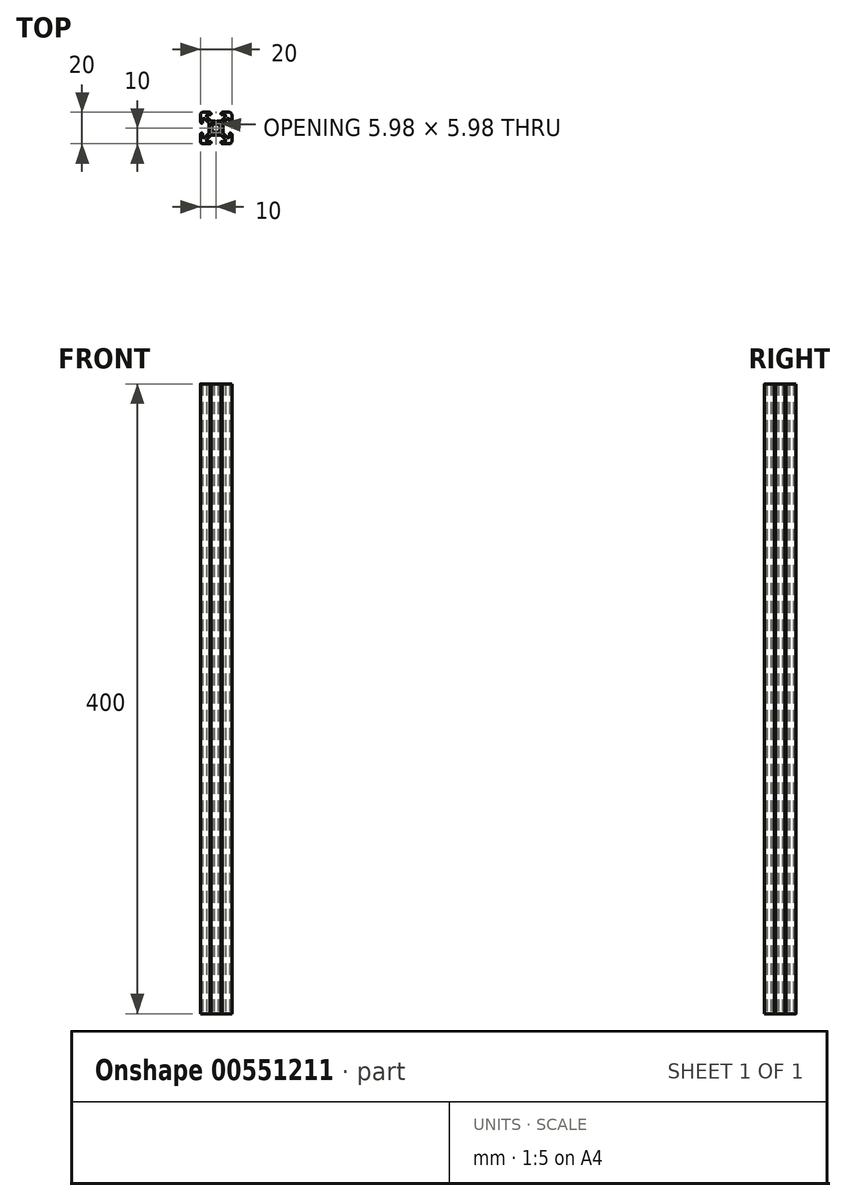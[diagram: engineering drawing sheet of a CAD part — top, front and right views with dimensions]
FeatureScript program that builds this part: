
annotation { "Feature Type Name" : "Feature", "Feature Type Description" : "" }
export const myFeature = defineFeature(function(context is Context, id is Id, definition is map)
    precondition{}
    {
        {
            var Q0;
            Q0=qCreatedBy(makeId("Top.planeOp"),FACE);
            var sketch = newSketch(context, id + "F0", { "sketchPlane" : qUnion([Q0])});
            skLineSegment(sketch, "E0.0", {"start": v(-0.95, 4.5) * mm, "end": v(-3.23, 4.5) * mm});
            skLineSegment(sketch, "E0.1", {"start": v(-3.59, 4.65) * mm, "end": v(-5.85, 6.91) * mm});
            skArc(sketch, "E0.2", {"start": v(-3.23, 4.5) * mm, "mid": v(-3.42, 4.54) * mm, "end": v(-3.59, 4.65) * mm});
            skArc(sketch, "E0.3", {"start": v(-4.65, 3.59) * mm, "mid": v(-4.54, 3.42) * mm, "end": v(-4.5, 3.23) * mm});
            skLineSegment(sketch, "E0.4", {"start": v(-6.91, 5.85) * mm, "end": v(-4.65, 3.59) * mm});
            skArc(sketch, "E0.5", {"start": v(-5.85, 6.91) * mm, "mid": v(-5.96, 7.08) * mm, "end": v(-6, 7.27) * mm});
            skLineSegment(sketch, "E0.6", {"start": v(-6, 7.27) * mm, "end": v(-6, 8) * mm});
            skArc(sketch, "E0.7", {"start": v(-6, 8) * mm, "mid": v(-5.85, 8.35) * mm, "end": v(-5.5, 8.5) * mm});
            skLineSegment(sketch, "E0.8", {"start": v(-5.5, 8.5) * mm, "end": v(-3.6, 8.5) * mm});
            skArc(sketch, "E0.9", {"start": v(-3.6, 8.5) * mm, "mid": v(-3.25, 8.65) * mm, "end": v(-3.1, 9) * mm});
            skLineSegment(sketch, "E0.10", {"start": v(-3.1, 9) * mm, "end": v(-3.1, 9.3) * mm});
            skArc(sketch, "E0.11", {"start": v(-3.1, 9.3) * mm, "mid": v(-3.16, 9.44) * mm, "end": v(-3.3, 9.5) * mm});
            skLineSegment(sketch, "E0.12", {"start": v(-3.3, 9.5) * mm, "end": v(-3.65, 9.5) * mm});
            skLineSegment(sketch, "E0.13", {"start": v(-3.65, 9.5) * mm, "end": v(-3.65, 9.8) * mm});
            skArc(sketch, "E0.14", {"start": v(-3.65, 9.8) * mm, "mid": v(-3.7, 9.94) * mm, "end": v(-3.85, 10) * mm});
            skLineSegment(sketch, "E0.15", {"start": v(-3.85, 10) * mm, "end": v(-8.5, 10) * mm});
            skArc(sketch, "E0.16", {"start": v(-7.27, 6) * mm, "mid": v(-7.08, 5.96) * mm, "end": v(-6.91, 5.85) * mm});
            skLineSegment(sketch, "E0.17", {"start": v(-8, 6) * mm, "end": v(-7.27, 6) * mm});
            skArc(sketch, "E0.18", {"start": v(-8.5, 5.5) * mm, "mid": v(-8.35, 5.85) * mm, "end": v(-8, 6) * mm});
            skLineSegment(sketch, "E0.19", {"start": v(-8.5, 3.6) * mm, "end": v(-8.5, 5.5) * mm});
            skArc(sketch, "E0.20", {"start": v(-9, 3.1) * mm, "mid": v(-8.65, 3.25) * mm, "end": v(-8.5, 3.6) * mm});
            skArc(sketch, "E0.21", {"start": v(-8.5, 10) * mm, "mid": v(-9.56, 9.56) * mm, "end": v(-10, 8.5) * mm});
            skLineSegment(sketch, "E0.22", {"start": v(-10, 8.5) * mm, "end": v(-10, 3.85) * mm});
            skArc(sketch, "E0.23", {"start": v(-10, 3.85) * mm, "mid": v(-9.94, 3.7) * mm, "end": v(-9.8, 3.65) * mm});
            skLineSegment(sketch, "E0.24", {"start": v(-9.8, 3.65) * mm, "end": v(-9.5, 3.65) * mm});
            skLineSegment(sketch, "E0.25", {"start": v(-9.5, 3.65) * mm, "end": v(-9.5, 3.3) * mm});
            skArc(sketch, "E0.26", {"start": v(-9.5, 3.3) * mm, "mid": v(-9.44, 3.16) * mm, "end": v(-9.3, 3.1) * mm});
            skLineSegment(sketch, "E0.27", {"start": v(-9.3, 3.1) * mm, "end": v(-9, 3.1) * mm});
            skLineSegment(sketch, "E0.28", {"start": v(-4.5, 3.23) * mm, "end": v(-4.5, 0.95) * mm});
            skLineSegment(sketch, "E0.29", {"start": v(-0.1, 4.04) * mm, "end": v(-0.85, 4.47) * mm});
            skArc(sketch, "E0.30", {"start": v(-0.85, 4.47) * mm, "mid": v(-0.9, 4.5) * mm, "end": v(-0.95, 4.5) * mm});
            skLineSegment(sketch, "E0.31", {"start": v(0.85, 4.47) * mm, "end": v(0.1, 4.04) * mm});
            skLineSegment(sketch, "E0.32", {"start": v(3.23, 4.5) * mm, "end": v(0.95, 4.5) * mm});
            skArc(sketch, "E0.33", {"start": v(0.95, 4.5) * mm, "mid": v(0.9, 4.5) * mm, "end": v(0.85, 4.47) * mm});
            skArc(sketch, "E0.34", {"start": v(0.1, 4.04) * mm, "mid": v(0, 4.01) * mm, "end": v(-0.1, 4.04) * mm});
            skLineSegment(sketch, "E0.35", {"start": v(5.85, 6.91) * mm, "end": v(3.59, 4.65) * mm});
            skLineSegment(sketch, "E0.36", {"start": v(6, 8) * mm, "end": v(6, 7.27) * mm});
            skArc(sketch, "E0.37", {"start": v(5.5, 8.5) * mm, "mid": v(5.85, 8.35) * mm, "end": v(6, 8) * mm});
            skLineSegment(sketch, "E0.38", {"start": v(3.6, 8.5) * mm, "end": v(5.5, 8.5) * mm});
            skArc(sketch, "E0.39", {"start": v(3.1, 9) * mm, "mid": v(3.25, 8.65) * mm, "end": v(3.6, 8.5) * mm});
            skLineSegment(sketch, "E0.40", {"start": v(8.5, 10) * mm, "end": v(3.85, 10) * mm});
            skArc(sketch, "E0.41", {"start": v(3.59, 4.65) * mm, "mid": v(3.42, 4.54) * mm, "end": v(3.23, 4.5) * mm});
            skArc(sketch, "E0.42", {"start": v(6, 7.27) * mm, "mid": v(5.96, 7.08) * mm, "end": v(5.85, 6.91) * mm});
            skLineSegment(sketch, "E0.43", {"start": v(3.1, 9.3) * mm, "end": v(3.1, 9) * mm});
            skArc(sketch, "E0.44", {"start": v(3.85, 10) * mm, "mid": v(3.7, 9.94) * mm, "end": v(3.65, 9.8) * mm});
            skLineSegment(sketch, "E0.45", {"start": v(3.65, 9.8) * mm, "end": v(3.65, 9.5) * mm});
            skLineSegment(sketch, "E0.46", {"start": v(3.65, 9.5) * mm, "end": v(3.3, 9.5) * mm});
            skArc(sketch, "E0.47", {"start": v(3.3, 9.5) * mm, "mid": v(3.16, 9.44) * mm, "end": v(3.1, 9.3) * mm});
            skArc(sketch, "E0.48", {"start": v(10, 8.5) * mm, "mid": v(9.56, 9.56) * mm, "end": v(8.5, 10) * mm});
            skLineSegment(sketch, "E0.49", {"start": v(10, 3.85) * mm, "end": v(10, 8.5) * mm});
            skArc(sketch, "E0.50", {"start": v(9.8, 3.65) * mm, "mid": v(9.94, 3.7) * mm, "end": v(10, 3.85) * mm});
            skLineSegment(sketch, "E0.51", {"start": v(9.5, 3.65) * mm, "end": v(9.8, 3.65) * mm});
            skLineSegment(sketch, "E0.52", {"start": v(9.5, 3.3) * mm, "end": v(9.5, 3.65) * mm});
            skArc(sketch, "E0.53", {"start": v(9.3, 3.1) * mm, "mid": v(9.44, 3.16) * mm, "end": v(9.5, 3.3) * mm});
            skArc(sketch, "E0.54", {"start": v(8.5, 3.6) * mm, "mid": v(8.65, 3.25) * mm, "end": v(9, 3.1) * mm});
            skLineSegment(sketch, "E0.55", {"start": v(8.5, 5.5) * mm, "end": v(8.5, 3.6) * mm});
            skArc(sketch, "E0.56", {"start": v(8, 6) * mm, "mid": v(8.35, 5.85) * mm, "end": v(8.5, 5.5) * mm});
            skLineSegment(sketch, "E0.57", {"start": v(7.27, 6) * mm, "end": v(8, 6) * mm});
            skArc(sketch, "E0.58", {"start": v(6.91, 5.85) * mm, "mid": v(7.08, 5.96) * mm, "end": v(7.27, 6) * mm});
            skLineSegment(sketch, "E0.59", {"start": v(4.65, 3.59) * mm, "end": v(6.91, 5.85) * mm});
            skArc(sketch, "E0.60", {"start": v(4.5, 3.23) * mm, "mid": v(4.54, 3.42) * mm, "end": v(4.65, 3.59) * mm});
            skLineSegment(sketch, "E0.61", {"start": v(9, 3.1) * mm, "end": v(9.3, 3.1) * mm});
            skLineSegment(sketch, "E0.62", {"start": v(4.5, 0.95) * mm, "end": v(4.5, 3.23) * mm});
            skLineSegment(sketch, "E0.63", {"start": v(4.04, 0.1) * mm, "end": v(4.47, 0.85) * mm});
            skArc(sketch, "E0.64", {"start": v(4.47, 0.85) * mm, "mid": v(4.5, 0.9) * mm, "end": v(4.5, 0.95) * mm});
            skArc(sketch, "E0.65", {"start": v(4.04, -0.1) * mm, "mid": v(4.01, 0) * mm, "end": v(4.04, 0.1) * mm});
            skLineSegment(sketch, "E0.66", {"start": v(4.47, -0.85) * mm, "end": v(4.04, -0.1) * mm});
            skArc(sketch, "E0.67", {"start": v(3, 1.9) * mm, "mid": v(2.51, 2.5) * mm, "end": v(1.91, 2.99) * mm});
            skLineSegment(sketch, "E0.68", {"start": v(1.91, 2.99) * mm, "end": v(1.26, 2.45) * mm});
            skLineSegment(sketch, "E0.69", {"start": v(2.45, 1.26) * mm, "end": v(3, 1.9) * mm});
            skArc(sketch, "E0.70", {"start": v(1.26, 2.45) * mm, "mid": v(0, 2.75) * mm, "end": v(-1.26, 2.45) * mm});
            skLineSegment(sketch, "E0.71", {"start": v(-1.26, 2.45) * mm, "end": v(-1.91, 2.99) * mm});
            skArc(sketch, "E0.72", {"start": v(2.45, -1.26) * mm, "mid": v(2.75, 0) * mm, "end": v(2.45, 1.26) * mm});
            skArc(sketch, "E0.73", {"start": v(-1.91, 2.99) * mm, "mid": v(-2.51, 2.5) * mm, "end": v(-3, 1.9) * mm});
            skLineSegment(sketch, "E0.74", {"start": v(-3, 1.9) * mm, "end": v(-2.45, 1.26) * mm});
            skArc(sketch, "E0.75", {"start": v(-2.45, 1.26) * mm, "mid": v(-2.75, 0) * mm, "end": v(-2.45, -1.26) * mm});
            skLineSegment(sketch, "E0.76", {"start": v(-2.45, -1.26) * mm, "end": v(-3, -1.9) * mm});
            skArc(sketch, "E0.77", {"start": v(-3, -1.9) * mm, "mid": v(-2.51, -2.5) * mm, "end": v(-1.91, -2.99) * mm});
            skLineSegment(sketch, "E0.78", {"start": v(-1.91, -2.99) * mm, "end": v(-1.26, -2.45) * mm});
            skArc(sketch, "E0.79", {"start": v(-1.26, -2.45) * mm, "mid": v(0, -2.75) * mm, "end": v(1.26, -2.45) * mm});
            skLineSegment(sketch, "E0.80", {"start": v(1.26, -2.45) * mm, "end": v(1.91, -2.99) * mm});
            skArc(sketch, "E0.81", {"start": v(1.91, -2.99) * mm, "mid": v(2.51, -2.5) * mm, "end": v(3, -1.9) * mm});
            skLineSegment(sketch, "E0.82", {"start": v(3, -1.9) * mm, "end": v(2.45, -1.26) * mm});
            skArc(sketch, "E0.83", {"start": v(4.5, -0.95) * mm, "mid": v(4.5, -0.9) * mm, "end": v(4.47, -0.85) * mm});
            skLineSegment(sketch, "E0.84", {"start": v(4.5, -3.23) * mm, "end": v(4.5, -0.95) * mm});
            skLineSegment(sketch, "E0.85", {"start": v(0.95, -4.5) * mm, "end": v(3.23, -4.5) * mm});
            skArc(sketch, "E0.86", {"start": v(4.65, -3.59) * mm, "mid": v(4.54, -3.42) * mm, "end": v(4.5, -3.23) * mm});
            skLineSegment(sketch, "E0.87", {"start": v(6.91, -5.85) * mm, "end": v(4.65, -3.59) * mm});
            skArc(sketch, "E0.88", {"start": v(3.23, -4.5) * mm, "mid": v(3.42, -4.54) * mm, "end": v(3.59, -4.65) * mm});
            skLineSegment(sketch, "E0.89", {"start": v(3.59, -4.65) * mm, "end": v(5.85, -6.91) * mm});
            skLineSegment(sketch, "E0.90", {"start": v(8, -6) * mm, "end": v(7.27, -6) * mm});
            skLineSegment(sketch, "E0.91", {"start": v(8.5, -3.6) * mm, "end": v(8.5, -5.5) * mm});
            skArc(sketch, "E0.92", {"start": v(8.5, -5.5) * mm, "mid": v(8.35, -5.85) * mm, "end": v(8, -6) * mm});
            skArc(sketch, "E0.93", {"start": v(7.27, -6) * mm, "mid": v(7.08, -5.96) * mm, "end": v(6.91, -5.85) * mm});
            skArc(sketch, "E0.94", {"start": v(9, -3.1) * mm, "mid": v(8.65, -3.25) * mm, "end": v(8.5, -3.6) * mm});
            skLineSegment(sketch, "E0.95", {"start": v(9.3, -3.1) * mm, "end": v(9, -3.1) * mm});
            skArc(sketch, "E0.96", {"start": v(9.5, -3.3) * mm, "mid": v(9.44, -3.16) * mm, "end": v(9.3, -3.1) * mm});
            skLineSegment(sketch, "E0.97", {"start": v(9.5, -3.65) * mm, "end": v(9.5, -3.3) * mm});
            skLineSegment(sketch, "E0.98", {"start": v(9.8, -3.65) * mm, "end": v(9.5, -3.65) * mm});
            skArc(sketch, "E0.99", {"start": v(10, -3.85) * mm, "mid": v(9.94, -3.7) * mm, "end": v(9.8, -3.65) * mm});
            skLineSegment(sketch, "E0.100", {"start": v(10, -8.5) * mm, "end": v(10, -3.85) * mm});
            skArc(sketch, "E0.101", {"start": v(8.5, -10) * mm, "mid": v(9.56, -9.56) * mm, "end": v(10, -8.5) * mm});
            skLineSegment(sketch, "E0.102", {"start": v(3.85, -10) * mm, "end": v(8.5, -10) * mm});
            skLineSegment(sketch, "E0.103", {"start": v(5.5, -8.5) * mm, "end": v(3.6, -8.5) * mm});
            skLineSegment(sketch, "E0.104", {"start": v(6, -7.27) * mm, "end": v(6, -8) * mm});
            skArc(sketch, "E0.105", {"start": v(5.85, -6.91) * mm, "mid": v(5.96, -7.08) * mm, "end": v(6, -7.27) * mm});
            skArc(sketch, "E0.106", {"start": v(6, -8) * mm, "mid": v(5.85, -8.35) * mm, "end": v(5.5, -8.5) * mm});
            skArc(sketch, "E0.107", {"start": v(3.6, -8.5) * mm, "mid": v(3.25, -8.65) * mm, "end": v(3.1, -9) * mm});
            skArc(sketch, "E0.108", {"start": v(3.65, -9.8) * mm, "mid": v(3.7, -9.94) * mm, "end": v(3.85, -10) * mm});
            skLineSegment(sketch, "E0.109", {"start": v(3.65, -9.5) * mm, "end": v(3.65, -9.8) * mm});
            skLineSegment(sketch, "E0.110", {"start": v(3.3, -9.5) * mm, "end": v(3.65, -9.5) * mm});
            skLineSegment(sketch, "E0.111", {"start": v(3.1, -9) * mm, "end": v(3.1, -9.3) * mm});
            skArc(sketch, "E0.112", {"start": v(3.1, -9.3) * mm, "mid": v(3.16, -9.44) * mm, "end": v(3.3, -9.5) * mm});
            skArc(sketch, "E0.113", {"start": v(0.85, -4.47) * mm, "mid": v(0.9, -4.5) * mm, "end": v(0.95, -4.5) * mm});
            skLineSegment(sketch, "E0.114", {"start": v(0.1, -4.04) * mm, "end": v(0.85, -4.47) * mm});
            skArc(sketch, "E0.115", {"start": v(-0.1, -4.04) * mm, "mid": v(0, -4.01) * mm, "end": v(0.1, -4.04) * mm});
            skLineSegment(sketch, "E0.116", {"start": v(-0.85, -4.47) * mm, "end": v(-0.1, -4.04) * mm});
            skArc(sketch, "E0.117", {"start": v(-0.95, -4.5) * mm, "mid": v(-0.9, -4.5) * mm, "end": v(-0.85, -4.47) * mm});
            skLineSegment(sketch, "E0.118", {"start": v(-3.23, -4.5) * mm, "end": v(-0.95, -4.5) * mm});
            skLineSegment(sketch, "E0.119", {"start": v(-5.85, -6.91) * mm, "end": v(-3.59, -4.65) * mm});
            skArc(sketch, "E0.120", {"start": v(-3.59, -4.65) * mm, "mid": v(-3.42, -4.54) * mm, "end": v(-3.23, -4.5) * mm});
            skArc(sketch, "E0.121", {"start": v(-6, -7.27) * mm, "mid": v(-5.96, -7.08) * mm, "end": v(-5.85, -6.91) * mm});
            skLineSegment(sketch, "E0.122", {"start": v(-6, -8) * mm, "end": v(-6, -7.27) * mm});
            skArc(sketch, "E0.123", {"start": v(-5.5, -8.5) * mm, "mid": v(-5.85, -8.35) * mm, "end": v(-6, -8) * mm});
            skLineSegment(sketch, "E0.124", {"start": v(-3.6, -8.5) * mm, "end": v(-5.5, -8.5) * mm});
            skArc(sketch, "E0.125", {"start": v(-3.1, -9) * mm, "mid": v(-3.25, -8.65) * mm, "end": v(-3.6, -8.5) * mm});
            skLineSegment(sketch, "E0.126", {"start": v(-3.1, -9.3) * mm, "end": v(-3.1, -9) * mm});
            skArc(sketch, "E0.127", {"start": v(-3.3, -9.5) * mm, "mid": v(-3.16, -9.44) * mm, "end": v(-3.1, -9.3) * mm});
            skLineSegment(sketch, "E0.128", {"start": v(-3.65, -9.5) * mm, "end": v(-3.3, -9.5) * mm});
            skLineSegment(sketch, "E0.129", {"start": v(-3.65, -9.8) * mm, "end": v(-3.65, -9.5) * mm});
            skArc(sketch, "E0.130", {"start": v(-3.85, -10) * mm, "mid": v(-3.7, -9.94) * mm, "end": v(-3.65, -9.8) * mm});
            skLineSegment(sketch, "E0.131", {"start": v(-8.5, -10) * mm, "end": v(-3.85, -10) * mm});
            skArc(sketch, "E0.132", {"start": v(-10, -8.5) * mm, "mid": v(-9.56, -9.56) * mm, "end": v(-8.5, -10) * mm});
            skLineSegment(sketch, "E0.133", {"start": v(-10, -3.85) * mm, "end": v(-10, -8.5) * mm});
            skLineSegment(sketch, "E0.134", {"start": v(-9.5, -3.65) * mm, "end": v(-9.8, -3.65) * mm});
            skArc(sketch, "E0.135", {"start": v(-9.8, -3.65) * mm, "mid": v(-9.94, -3.7) * mm, "end": v(-10, -3.85) * mm});
            skLineSegment(sketch, "E0.136", {"start": v(-9.5, -3.3) * mm, "end": v(-9.5, -3.65) * mm});
            skLineSegment(sketch, "E0.137", {"start": v(-9, -3.1) * mm, "end": v(-9.3, -3.1) * mm});
            skArc(sketch, "E0.138", {"start": v(-9.3, -3.1) * mm, "mid": v(-9.44, -3.16) * mm, "end": v(-9.5, -3.3) * mm});
            skArc(sketch, "E0.139", {"start": v(-8.5, -3.6) * mm, "mid": v(-8.65, -3.25) * mm, "end": v(-9, -3.1) * mm});
            skLineSegment(sketch, "E0.140", {"start": v(-8.5, -5.5) * mm, "end": v(-8.5, -3.6) * mm});
            skLineSegment(sketch, "E0.141", {"start": v(-7.27, -6) * mm, "end": v(-8, -6) * mm});
            skArc(sketch, "E0.142", {"start": v(-8, -6) * mm, "mid": v(-8.35, -5.85) * mm, "end": v(-8.5, -5.5) * mm});
            skArc(sketch, "E0.143", {"start": v(-6.91, -5.85) * mm, "mid": v(-7.08, -5.96) * mm, "end": v(-7.27, -6) * mm});
            skLineSegment(sketch, "E0.144", {"start": v(-4.65, -3.59) * mm, "end": v(-6.91, -5.85) * mm});
            skLineSegment(sketch, "E0.145", {"start": v(-4.5, -0.95) * mm, "end": v(-4.5, -3.23) * mm});
            skArc(sketch, "E0.146", {"start": v(-4.5, -3.23) * mm, "mid": v(-4.54, -3.42) * mm, "end": v(-4.65, -3.59) * mm});
            skLineSegment(sketch, "E0.147", {"start": v(-4.04, -0.1) * mm, "end": v(-4.47, -0.85) * mm});
            skLineSegment(sketch, "E0.148", {"start": v(-4.47, 0.85) * mm, "end": v(-4.04, 0.1) * mm});
            skArc(sketch, "E0.149", {"start": v(-4.04, 0.1) * mm, "mid": v(-4.01, 0) * mm, "end": v(-4.04, -0.1) * mm});
            skArc(sketch, "E0.150", {"start": v(-4.47, -0.85) * mm, "mid": v(-4.5, -0.9) * mm, "end": v(-4.5, -0.95) * mm});
            skArc(sketch, "E0.151", {"start": v(-4.5, 0.95) * mm, "mid": v(-4.5, 0.9) * mm, "end": v(-4.47, 0.85) * mm});
            skSolve(sketch);
        }
        {
            var Q0;
            Q0=qSketchRegion(id+"F0",true);
            extrude(context, id + "F1", {"entities" : qUnion([Q0]), "depth" : 400 * mm, "offsetDistance" : 25 * mm});
        }
    });
